# Revit family: Hager-FW-Surface_mounted-IP30-With_Cover-With_DIN-Hosted-PL-pl
name_source: partatom
category: Electrical Equipment
units: mm (PartAtom-declared; Revit-internal decimal feet)

## family parameters
Cut with Voids When Loaded = No
Host = Face
Maintain Annotation Orientation = Yes
Panel Configuration = Two Columns, Circuits Across
Part Type = Panelboard
Room Calculation Point = No
Round Connector Dimension = Use Diameter
Shared = No

## types (12) — shared parameters
BC_MODEL_ID = 1554259
BC_OBJECT_ID = 513844
BC_OBJECT_VERSION = #5
Code hager = ADD-EC000214_EU
EF000003 - Sposób montażu = Montaż natynkowy
EF000007 - Kolor = Biały
EF000024 - Odporność na promieniowanie UV = No
EF000049 - Głębokość = 150 mm
EF000116 - Numer RAL = 9010
EF000118 - Z płytą montażową = No
EF001062 - Wykonanie zgodne z Dyrektywą Kompatybilności Elektromagnetycznej EMC = No
EF001088 - Możliwość rozbudowy = Yes
EF001134 - Szyna DIN = Yes
EF004462 - Rodzaj zamknięcia = Inne
EF005474 - Stopień ochrony (IP) = IP30
EF006244 - Transparentna pokrywa/drzwi = No
EF006306 - Z zamkiem = No
EF009212 - Wykonanie/rodzaj pokrywy = Zamknięty
EF015776 - Listwa zaciskowa uziemienia = Yes
EF015777 - Listwa zaciskowa przewodu neutralnego = No
EF015941 - Drzwi przepuszczające sygnał = No
ETIM class code = EC000214
ETIM class name = Small distribution board
HG000001-Number of columns-pl = 1
HG000002-with door or cover-pl = Yes
HG000003-Range-pl = FW
HG000005-Thickness-pl = 2 mm  [stored 0.00656168 ft]
HG000006-Flush mounted-pl = No
HG000009-Double swing door-pl = No
HG000010-Asymmetric doors-pl = No
HG000011-Empty rows from bottom-pl = No
HG000012-Door swing angle-pl = 90.00°
HG000013-Door on the left-pl = No
HG000014-Door on the right-pl = Yes
HG000015-Clearance visibility-pl = Yes
HG000016-Door 3D visibility-pl = Yes
HG000017-Distance between poles-pl = 18 mm  [stored 0.0590551 ft]
HG000060-RAL-number = 9010
HG000099-Onfly Template ID-pl-PL = 507532
Manufacturer = Hager
Name = FW-Surface_mounted-IP30-With_Cover-With_DIN-PL
Name BIM&CO = Electricity
Name hager = ADD_Enclosures_EC000214
Uniformat = Low Tension Service & Dist.
Uniformat code = D501001
zero-valued in all types: Default Elevation, EF000218 - Głębokość wbudowania, EF000332 - Wysokość wbudowania, EF000846 - Szerokość wbudowania, EF001131 - Głębokość wewnętrzna, HG000007-Number of empty columns-pl, HG000008-Number of empty rows-pl

## per-type parameters (varying)
| type | BC_VARIANT_ID | EF000008 - Szerokość | EF000040 - Wysokość | EF000266 - Liczba rzędów | EF002950 - Szerokość wyrażona liczbą modułów | HG000004-Manufacturer reference-pl | HGEF000266-Liczba rzędów | HGEF0002950-Szerokość wyrażona liczbą modułów |
| FW-Surface_mounted_W355_H641_D150_12_Modular_Spacing-FW312WT | 1178675 | 355 mm | 641 mm  [stored 2.10302 ft] | 3 | 12 | FW312WT | 3 | 12 |
| FW-Surface_mounted_W571_H641_D150_24_Modular_Spacing-FW324WT | 1178676 | 571 mm  [stored 1.87336 ft] | 641 mm  [stored 2.10302 ft] | 3 | 24 | FW324WT | 3 | 24 |
| FW-Surface_mounted_W355_H791_D150_12_Modular_Spacing-FW412WT | 1178677 | 355 mm | 791 mm | 4 | 12 | FW412WT | 4 | 12 |
| FW-Surface_mounted_W571_H791_D150_24_Modular_Spacing-FW424WT | 1178678 | 571 mm  [stored 1.87336 ft] | 791 mm | 4 | 24 | FW424WT | 4 | 24 |
| FW-Surface_mounted_W787_H791_D150_36_Modular_Spacing-FW436WT | 1178679 | 787 mm  [stored 2.58202 ft] | 791 mm | 4 | 36 | FW436WT | 4 | 36 |
| FW-Surface_mounted_W355_H941_D150_12_Modular_Spacing-FW512WT | 1178680 | 355 mm | 941 mm | 5 | 12 | FW512WT | 5 | 12 |
| FW-Surface_mounted_W571_H941_D150_24_Modular_Spacing-FW524WT | 1178681 | 571 mm  [stored 1.87336 ft] | 941 mm | 5 | 24 | FW524WT | 5 | 24 |
| FW-Surface_mounted_W787_H941_D150_36_Modular_Spacing-FW536WT | 1178682 | 787 mm  [stored 2.58202 ft] | 941 mm | 5 | 36 | FW536WT | 5 | 36 |
| FW-Surface_mounted_W355_H1091_D150_12_Modular_Spacing-FW612WT | 1178683 | 355 mm | 1091 mm | 6 | 12 | FW612WT | 6 | 12 |
| FW-Surface_mounted_W571_H1091_D150_24_Modular_Spacing-FW624WT | 1178684 | 571 mm  [stored 1.87336 ft] | 1091 mm | 6 | 24 | FW624WT | 6 | 24 |
| FW-Surface_mounted_W787_H1091_D150_36_Modular_Spacing-FW636WT | 1178685 | 787 mm  [stored 2.58202 ft] | 1091 mm | 6 | 36 | FW636WT | 6 | 36 |
| FW-Surface_mounted_W787_H1241_D150_36_Modular_Spacing-FW736WT | 1178686 | 787 mm  [stored 2.58202 ft] | 1241 mm  [stored 4.07152 ft] | 7 | 36 | FW736WT | 7 | 36 |

note: column(s) folded — value = type name in every type: Reference

note: [stored X ft] marks values corroborated as IEEE doubles in the binary element streams (Revit-internal decimal feet)

## geometry (parser evidence)
native form markers: Sweep x16
no freeform markers — native parametric forms only
